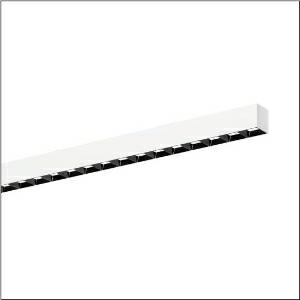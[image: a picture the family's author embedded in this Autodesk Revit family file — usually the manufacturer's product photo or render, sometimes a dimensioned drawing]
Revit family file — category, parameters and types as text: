
# Revit family: silica_r__21_51mx24tat4w_113b
name_source: partatom
category: Lighting Fixtures
units: mm (PartAtom-declared; Revit-internal decimal feet)

## family parameters
Cut with Voids When Loaded = No
Host = Face
Light Source = No
Part Type = Normal
Room Calculation Point = No
Round Connector Dimension = Use Diameter
Shared = No

## types (1)
- --- (1 x LED, 3280 lm, 32.4 W, 6500K)
    Apparent Load = 32 VA
    CIE Flux Codes = 74 94 99 100 100
    Color Rendering = 80
    Color Temperature = 6500K
    Default Elevation = 1800 mm
    Description = Silica® 21, office luminaire, primary light control with darklight reflector, of PMMA, black, light emission: direct distribution, primary light characteristic: asymmetric, installation type: surface-mounted, LED, rated luminous flux: 3.280lm, luminous efficacy: 96lm/W, light colour: 8tw, colour temperature: 2700..6500K, control gear: DALI DT8, with terminal, 3+2-pole, max. 2.5mm², mains connection: 220..240V, AC, 50/60Hz, rated input power: 34.1W, luminaire housing, of aluminium, traffic white (RAL 9016), length: 1.204mm, width: 53mm, height: 53mm, protection rating (complete): IP20, insulation class (complete): insulation class I (protective earthing), certification: CE, permissible operating ambient temperature: 0..+35°C, standard: EN 50419, packaging unit: 1 piece
    Height = 53 mm
    Lamp = 1 x LED
    Lamp Light Flux = 3280 lm
    Lamp Power = 32.4 W
    Lamp count = 1
    Length = 1204 mm
    Luminous efficacy = 101 lm/W
    Manufacturer = Siteco
    ModVariant = No
    Model = 51MX24TAT4W
    Mounting Place = Ceiling
    Mounting Type = Surface mounted
    Number of Poles = 1
    OnlyDefault = Yes
    Power Factor = 1
    Product Name = Silica® 21
    Product group = office luminaire | ceiling mounted
    ProductGroupID = 302
    Protection Class = Protection class I
    Protection Degree = IP 20
    RLX_Detail_Level = 1
    RLX_Emergency_Light_Flux = 0 lm
    RLX_Emergency_Type = 0
    RLX_Emergency_Type_DB = No
    RlxData = <blob elided: 38349 chars, md5=df0ddc70>
    Socket = socket
    Standby Power = 0 W
    System Light Flux = 3280 lm
    System Power = 32 W
    Type Comments = individual setting
    Type Image = l_1335873.jpg
    URL = http://relux.com
    VarID = @adj_140016
    Voltage = 0 V
    Weight = 0.00 kg
    Width = 53 mm

## geometry (parser evidence)
native form markers: Blend x4, Sweep x9
no freeform markers — native parametric forms only
